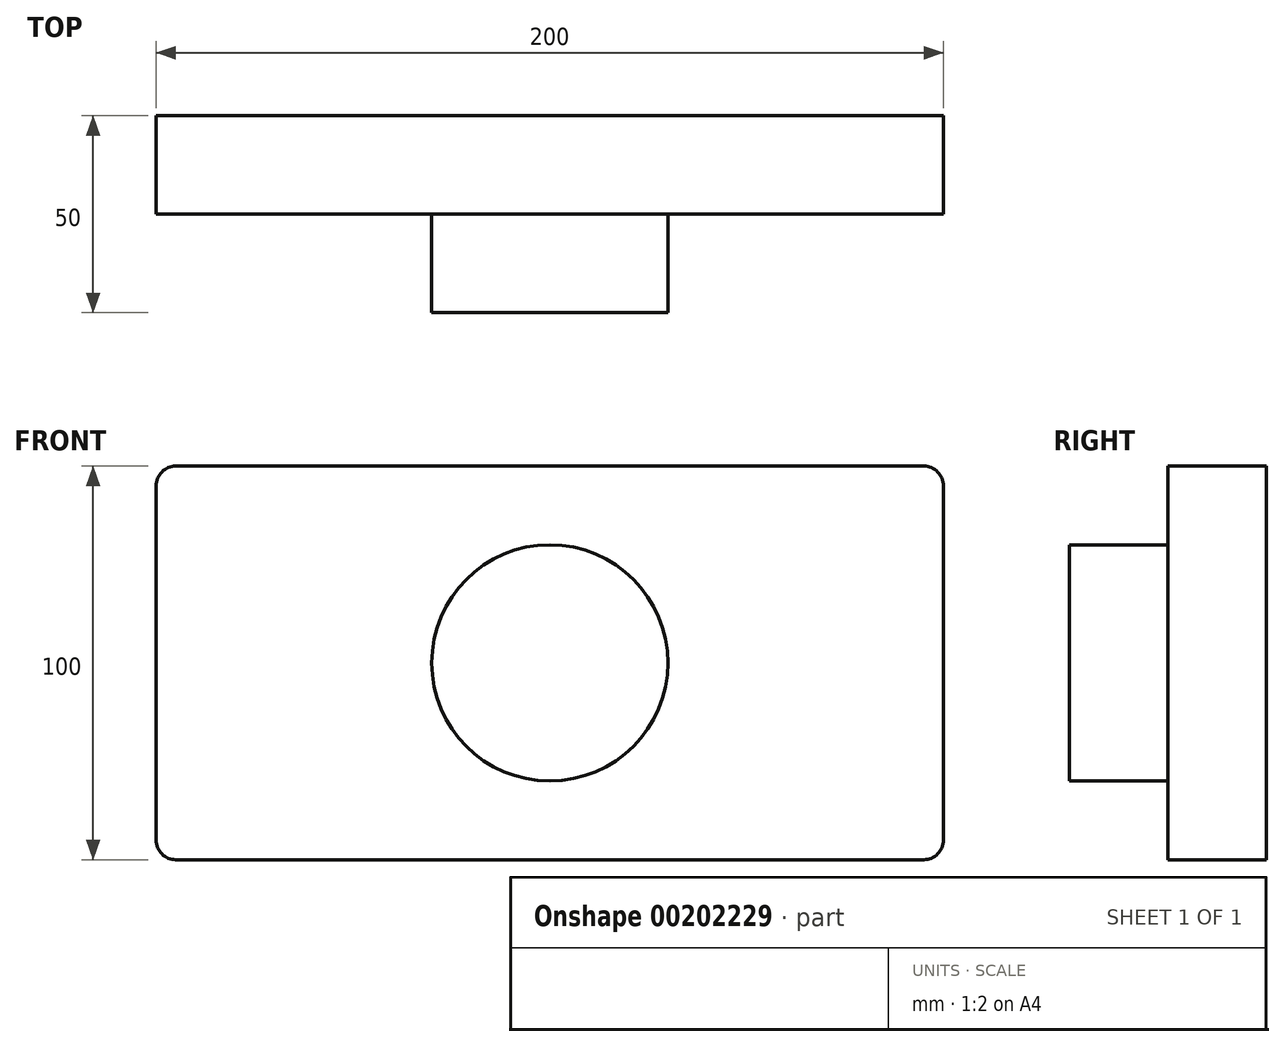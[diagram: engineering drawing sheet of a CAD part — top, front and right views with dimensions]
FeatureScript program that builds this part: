
annotation { "Feature Type Name" : "Feature", "Feature Type Description" : "" }
export const myFeature = defineFeature(function(context is Context, id is Id, definition is map)
    precondition{}
    {
        {
            var Q0;
            Q0=qCreatedBy(makeId("Front.planeOp"),FACE);
            var sketch = newSketch(context, id + "F0", { "sketchPlane" : qUnion([Q0])});
            skLineSegment(sketch, "E0.bottom", {"start": v(100, -50) * mm, "end": v(-100, -50) * mm});
            skLineSegment(sketch, "E0.top", {"start": v(100, 50) * mm, "end": v(-100, 50) * mm});
            skLineSegment(sketch, "E0.left", {"start": v(100, -50) * mm, "end": v(100, 50) * mm});
            skLineSegment(sketch, "E0.right", {"start": v(-100, -50) * mm, "end": v(-100, 50) * mm});
            skPoint(sketch, "E0.middle", {"position": v(0, 0) * mm});
            skSolve(sketch);
        }
        {
            var Q0;
            Q0=makeQuery(id+"F0.imprint","IMPRINT",FACE,{"disambiguationData":[TD([[makeQuery(id+"F0.imprint","IMPRINT",EDGE,{"derivedFrom":sQuery(id+"F0.wireOp",EDGE,"E0.bottom")}),-1.0]])]});
            extrude(context, id + "F1", {"entities" : qUnion([Q0]), "depth" : 25 * mm});
        }
        {
            var Q0;
            Q0=makeQuery(id+"F1.opExtrude","SWEPT_EDGE",EDGE,{"disambiguationData":[OSD([sQuery(id+"F0.wireOp",EDGE,"E0.bottom"),sQuery(id+"F0.wireOp",EDGE,"E0.right")])]});
            var Q1;
            Q1=makeQuery(id+"F1.opExtrude","SWEPT_EDGE",EDGE,{"disambiguationData":[OSD([sQuery(id+"F0.wireOp",EDGE,"E0.bottom"),sQuery(id+"F0.wireOp",EDGE,"E0.left")])]});
            var Q2;
            Q2=makeQuery(id+"F1.opExtrude","SWEPT_EDGE",EDGE,{"disambiguationData":[OSD([sQuery(id+"F0.wireOp",EDGE,"E0.top"),sQuery(id+"F0.wireOp",EDGE,"E0.left")])]});
            var Q3;
            Q3=makeQuery(id+"F1.opExtrude","SWEPT_EDGE",EDGE,{"disambiguationData":[OSD([sQuery(id+"F0.wireOp",EDGE,"E0.top"),sQuery(id+"F0.wireOp",EDGE,"E0.right")])]});
            fillet(context, id + "F2", {"entities" : qUnion([Q0, Q1, Q2, Q3]), "radius" : 5 * mm, "tangentPropagation" : true, "allowEdgeOverflow" : false});
        }
        {
            var Q0;
            Q0=makeQuery(id+"F1.opExtrude","CAP_FACE",FACE,{"disambiguationData":[OSD([sQuery(id+"F0.wireOp",EDGE,"E0.bottom"),sQuery(id+"F0.wireOp",EDGE,"E0.top"),sQuery(id+"F0.wireOp",EDGE,"E0.left"),sQuery(id+"F0.wireOp",EDGE,"E0.right")])],"isStart":false});
            var sketch = newSketch(context, id + "F3", { "sketchPlane" : qUnion([Q0])});
            skCircle(sketch, "E1", {"center": v(0, 0) * mm, "radius": 30 * mm});
            skSolve(sketch);
        }
        {
            var Q0;
            Q0=makeQuery(id+"F3.imprint","IMPRINT",FACE,{"disambiguationData":[TD([[makeQuery(id+"F3.imprint","IMPRINT",EDGE,{"derivedFrom":sQuery(id+"F3.wireOp",EDGE,"E1")}),1.0]])]});
            extrude(context, id + "F4", {"entities" : qUnion([Q0]), "operationType" : NewBodyOperationType.ADD, "depth" : 25 * mm});
        }
    });
